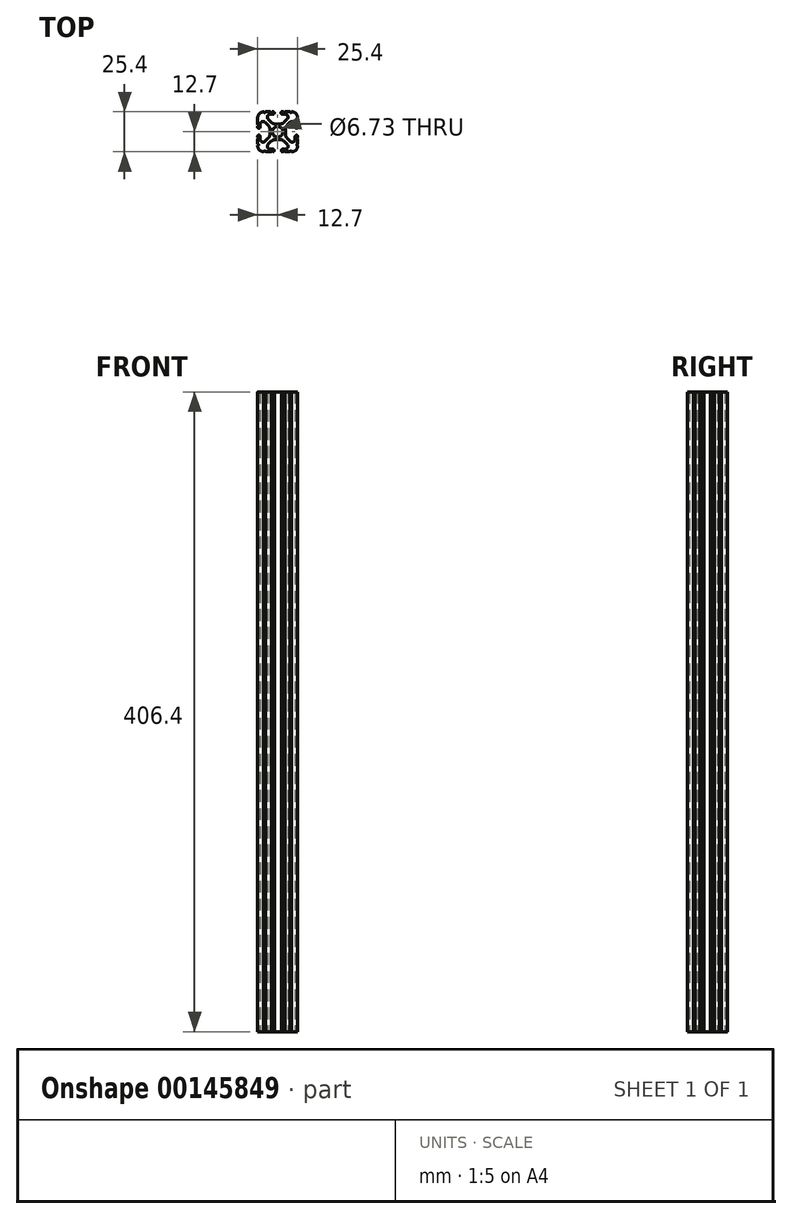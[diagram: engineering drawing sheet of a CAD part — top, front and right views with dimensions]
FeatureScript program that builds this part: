
annotation { "Feature Type Name" : "Feature", "Feature Type Description" : "" }
export const myFeature = defineFeature(function(context is Context, id is Id, definition is map)
    precondition{}
    {
        {
            var Q0;
            Q0=qCreatedBy(makeId("Top.planeOp"),FACE);
            var sketch = newSketch(context, id + "F0", { "sketchPlane" : qUnion([Q0])});
            skCircle(sketch, "E0", {"center": v(-12.7, 12.7) * mm, "radius": 3.36 * mm});
            skLineSegment(sketch, "E1.bottom", {"start": v(-11.24, 17.64) * mm, "end": v(-14.16, 17.64) * mm});
            skLineSegment(sketch, "E1.top", {"start": v(-11.24, 7.76) * mm, "end": v(-14.16, 7.76) * mm});
            skLineSegment(sketch, "E1.left", {"start": v(-7.76, 14.16) * mm, "end": v(-7.76, 11.24) * mm});
            skLineSegment(sketch, "E1.right", {"start": v(-17.64, 14.16) * mm, "end": v(-17.64, 11.24) * mm});
            skPoint(sketch, "E2.visualSharp", {"position": v(-25.4, 25.4) * mm});
            skPoint(sketch, "E3.visualSharp", {"position": v(0, 25.4) * mm});
            skPoint(sketch, "E4.visualSharp", {"position": v(0, 0) * mm});
            skPoint(sketch, "E5.visualSharp", {"position": v(-25.4, 0) * mm});
            skLineSegment(sketch, "E6.0", {"start": v(-18.7, 20.6) * mm, "end": v(-16.85, 18.76) * mm});
            skLineSegment(sketch, "E7.0", {"start": v(-20.6, 18.7) * mm, "end": v(-18.76, 16.85) * mm});
            skPoint(sketch, "E8.orphan", {"position": v(-23.85, 1.55) * mm});
            skPoint(sketch, "E9.orphan", {"position": v(-23.85, 23.85) * mm});
            skPoint(sketch, "E10.orphan", {"position": v(-1.55, 23.85) * mm});
            skPoint(sketch, "E11.orphan", {"position": v(-1.55, 1.55) * mm});
            skLineSegment(sketch, "E12", {"start": v(-8.55, 6.64) * mm, "end": v(-6.7, 4.8) * mm});
            skLineSegment(sketch, "E13.0", {"start": v(-18.7, 4.8) * mm, "end": v(-16.85, 6.64) * mm});
            skLineSegment(sketch, "E14.0", {"start": v(-20.6, 6.7) * mm, "end": v(-18.76, 8.55) * mm});
            skLineSegment(sketch, "E15.0", {"start": v(-8.55, 18.76) * mm, "end": v(-6.7, 20.6) * mm});
            skPoint(sketch, "E16.visualSharp", {"position": v(-23.85, 21.95) * mm});
            skArc(sketch, "E16.filletArc", {"start": v(-20.6, 18.7) * mm, "mid": v(-22.68, 19.1) * mm, "end": v(-23.85, 17.35) * mm});
            skPoint(sketch, "E17.visualSharp", {"position": v(-21.95, 23.85) * mm});
            skArc(sketch, "E17.filletArc", {"start": v(-17.35, 23.85) * mm, "mid": v(-19.1, 22.68) * mm, "end": v(-18.7, 20.6) * mm});
            skPoint(sketch, "E18.visualSharp", {"position": v(-5.34, 23.85) * mm});
            skLineSegment(sketch, "E19", {"start": v(-17.35, 23.85) * mm, "end": v(-15.58, 23.85) * mm});
            skLineSegment(sketch, "E20", {"start": v(-23.85, 17.35) * mm, "end": v(-23.85, 15.62) * mm});
            skLineSegment(sketch, "E21", {"start": v(-8.05, 1.55) * mm, "end": v(-9.78, 1.55) * mm});
            skArc(sketch, "E22.filletArc", {"start": v(-6.7, 20.6) * mm, "mid": v(-6.3, 22.68) * mm, "end": v(-8.05, 23.85) * mm});
            skPoint(sketch, "E23.visualSharp", {"position": v(-1.55, 3.45) * mm});
            skPoint(sketch, "E24.visualSharp", {"position": v(-3.45, 1.55) * mm});
            skArc(sketch, "E24.filletArc", {"start": v(-8.05, 1.55) * mm, "mid": v(-6.3, 2.73) * mm, "end": v(-6.7, 4.8) * mm});
            skArc(sketch, "E25.filletArc", {"start": v(-18.7, 4.8) * mm, "mid": v(-19.1, 2.73) * mm, "end": v(-17.35, 1.55) * mm});
            skArc(sketch, "E26.filletArc", {"start": v(-23.85, 8.05) * mm, "mid": v(-22.68, 6.3) * mm, "end": v(-20.6, 6.7) * mm});
            skLineSegment(sketch, "E27.bottom", {"start": v(-4.9, 0) * mm, "end": v(-8.05, 0) * mm});
            skLineSegment(sketch, "E27.top", {"start": v(-4.92, 25.4) * mm, "end": v(-8.05, 25.4) * mm});
            skLineSegment(sketch, "E27.left", {"start": v(0, 4.9) * mm, "end": v(0, 8.05) * mm});
            skLineSegment(sketch, "E27.right", {"start": v(-25.4, 4.9) * mm, "end": v(-25.4, 8.05) * mm});
            skArc(sketch, "E28.filletArc", {"start": v(-25.4, 3.81) * mm, "mid": v(-24.28, 1.12) * mm, "end": v(-21.59, 0) * mm});
            skArc(sketch, "E29.filletArc", {"start": v(-3.81, 0) * mm, "mid": v(-1.12, 1.12) * mm, "end": v(0, 3.8) * mm});
            skArc(sketch, "E30.filletArc", {"start": v(0, 21.59) * mm, "mid": v(-1.12, 24.28) * mm, "end": v(-3.8, 25.4) * mm});
            skArc(sketch, "E31.filletArc", {"start": v(-21.59, 25.4) * mm, "mid": v(-24.28, 24.28) * mm, "end": v(-25.4, 21.59) * mm});
            skPoint(sketch, "E32.newPointA", {"position": v(-17.64, 7.76) * mm});
            skArc(sketch, "E32.filletArc", {"start": v(-14.16, 7.76) * mm, "mid": v(-15.62, 7.47) * mm, "end": v(-16.85, 6.64) * mm});
            skPoint(sketch, "E33.newPointA", {"position": v(-7.76, 7.76) * mm});
            skArc(sketch, "E33.filletArc", {"start": v(-8.55, 6.64) * mm, "mid": v(-9.78, 7.47) * mm, "end": v(-11.24, 7.76) * mm});
            skArc(sketch, "E34.filletArc", {"start": v(-7.76, 11.24) * mm, "mid": v(-7.47, 9.78) * mm, "end": v(-6.64, 8.55) * mm});
            skArc(sketch, "E35.filletArc", {"start": v(-6.64, 16.85) * mm, "mid": v(-7.47, 15.62) * mm, "end": v(-7.76, 14.16) * mm});
            skPoint(sketch, "E36.newPointB", {"position": v(-7.76, 17.64) * mm});
            skArc(sketch, "E36.filletArc", {"start": v(-11.24, 17.64) * mm, "mid": v(-9.78, 17.93) * mm, "end": v(-8.55, 18.76) * mm});
            skPoint(sketch, "E37.newPointB", {"position": v(-17.64, 17.64) * mm});
            skArc(sketch, "E37.filletArc", {"start": v(-16.85, 18.76) * mm, "mid": v(-15.62, 17.93) * mm, "end": v(-14.16, 17.64) * mm});
            skArc(sketch, "E38.filletArc", {"start": v(-17.64, 14.16) * mm, "mid": v(-17.93, 15.62) * mm, "end": v(-18.76, 16.85) * mm});
            skArc(sketch, "E39.filletArc", {"start": v(-18.76, 8.55) * mm, "mid": v(-17.93, 9.78) * mm, "end": v(-17.64, 11.24) * mm});
            skLineSegment(sketch, "E40", {"start": v(-6.64, 8.55) * mm, "end": v(-4.8, 6.7) * mm});
            skPoint(sketch, "E41.visualSharp", {"position": v(-1.55, 21.95) * mm});
            skArc(sketch, "E42.filletArc", {"start": v(-4.8, 6.7) * mm, "mid": v(-2.73, 6.3) * mm, "end": v(-1.55, 8.05) * mm});
            skLineSegment(sketch, "E43", {"start": v(-1.55, 8.05) * mm, "end": v(-1.55, 9.78) * mm});
            skLineSegment(sketch, "E44", {"start": v(-6.64, 16.85) * mm, "end": v(-4.8, 18.7) * mm});
            skArc(sketch, "E45.filletArc", {"start": v(-1.55, 17.35) * mm, "mid": v(-2.73, 19.1) * mm, "end": v(-4.8, 18.7) * mm});
            skArc(sketch, "E46", {"start": v(-23.85, 9.78) * mm, "mid": v(-24.63, 10.56) * mm, "end": v(-25.4, 9.78) * mm});
            skArc(sketch, "E47", {"start": v(-25.4, 15.62) * mm, "mid": v(-24.63, 14.86) * mm, "end": v(-23.85, 15.62) * mm});
            skArc(sketch, "E48", {"start": v(-15.62, 23.85) * mm, "mid": v(-14.83, 24.63) * mm, "end": v(-15.62, 25.4) * mm});
            skArc(sketch, "E49", {"start": v(-9.78, 25.4) * mm, "mid": v(-10.6, 24.63) * mm, "end": v(-9.78, 23.85) * mm});
            skArc(sketch, "E50", {"start": v(-1.55, 15.62) * mm, "mid": v(-0.77, 14.88) * mm, "end": v(0, 15.62) * mm});
            skArc(sketch, "E51", {"start": v(0, 9.78) * mm, "mid": v(-0.77, 10.5) * mm, "end": v(-1.55, 9.78) * mm});
            skArc(sketch, "E52", {"start": v(-9.78, 1.55) * mm, "mid": v(-10.4, 0.77) * mm, "end": v(-9.78, 0) * mm});
            skArc(sketch, "E53", {"start": v(-15.62, 0) * mm, "mid": v(-14.85, 0.77) * mm, "end": v(-15.62, 1.55) * mm});
            skLineSegment(sketch, "E54.trimOffspring", {"start": v(-15.62, 1.55) * mm, "end": v(-17.35, 1.55) * mm});
            skLineSegment(sketch, "E55.trimOffspring", {"start": v(-16.7, 0) * mm, "end": v(-20.5, 0) * mm});
            skLineSegment(sketch, "E56.trimOffspring", {"start": v(-1.55, 15.62) * mm, "end": v(-1.55, 17.35) * mm});
            skLineSegment(sketch, "E57.trimOffspring", {"start": v(0, 15.62) * mm, "end": v(0, 16.26) * mm});
            skLineSegment(sketch, "E58.trimOffspring", {"start": v(-23.85, 9.78) * mm, "end": v(-23.85, 8.05) * mm});
            skLineSegment(sketch, "E59.trimOffspring", {"start": v(-25.4, 15.62) * mm, "end": v(-25.4, 16.26) * mm});
            skLineSegment(sketch, "E60.trimOffspring", {"start": v(-9.86, 23.85) * mm, "end": v(-8.05, 23.85) * mm});
            skLineSegment(sketch, "E61.trimOffspring", {"start": v(-15.58, 25.4) * mm, "end": v(-16.25, 25.4) * mm});
            skPoint(sketch, "E62.start.orphan", {"position": v(-15.62, 17.93) * mm});
            skPoint(sketch, "E63.start.orphan", {"position": v(-9.78, 17.93) * mm});
            skPoint(sketch, "E64.start.orphan", {"position": v(-7.47, 15.62) * mm});
            skPoint(sketch, "E65.start.orphan", {"position": v(-7.47, 9.78) * mm});
            skPoint(sketch, "E66.start.orphan", {"position": v(-17.93, 15.62) * mm});
            skPoint(sketch, "E67.start.orphan", {"position": v(-17.93, 9.78) * mm});
            skPoint(sketch, "E68.start.orphan", {"position": v(-9.78, 7.47) * mm});
            skPoint(sketch, "E69.start.orphan", {"position": v(-15.62, 7.47) * mm});
            skPoint(sketch, "E70.endSnap0", {"position": v(0, 18.6) * mm});
            skPoint(sketch, "E71.startSnap0", {"position": v(-1.55, 8.92) * mm});
            skArc(sketch, "E72", {"start": v(-4.92, 25.4) * mm, "mid": v(-4.37, 24.9) * mm, "end": v(-3.81, 25.4) * mm});
            skArc(sketch, "E73", {"start": v(-9.14, 25.4) * mm, "mid": v(-8.6, 24.86) * mm, "end": v(-8.05, 25.4) * mm});
            skArc(sketch, "E74", {"start": v(-17.35, 25.4) * mm, "mid": v(-16.8, 24.86) * mm, "end": v(-16.25, 25.4) * mm});
            skArc(sketch, "E75", {"start": v(-21.59, 25.4) * mm, "mid": v(-21.04, 24.85) * mm, "end": v(-20.49, 25.4) * mm});
            skLineSegment(sketch, "E76", {"start": v(-25.4, 21.59) * mm, "end": v(-25.4, 20.5) * mm});
            skArc(sketch, "E77", {"start": v(-25.4, 16.26) * mm, "mid": v(-24.84, 16.8) * mm, "end": v(-25.4, 17.35) * mm});
            skArc(sketch, "E78", {"start": v(-25.4, 8.05) * mm, "mid": v(-24.9, 8.6) * mm, "end": v(-25.4, 9.15) * mm});
            skArc(sketch, "E79", {"start": v(-25.4, 3.81) * mm, "mid": v(-24.85, 4.36) * mm, "end": v(-25.4, 4.9) * mm});
            skArc(sketch, "E80", {"start": v(-20.5, 0) * mm, "mid": v(-21.04, 0.55) * mm, "end": v(-21.59, 0) * mm});
            skArc(sketch, "E81", {"start": v(-15.62, 0) * mm, "mid": v(-16.16, 0.54) * mm, "end": v(-16.7, 0) * mm});
            skArc(sketch, "E82", {"start": v(-8.05, 0) * mm, "mid": v(-8.6, 0.55) * mm, "end": v(-9.15, 0) * mm});
            skArc(sketch, "E83", {"start": v(-3.81, 0) * mm, "mid": v(-4.35, 0.54) * mm, "end": v(-4.9, 0) * mm});
            skLineSegment(sketch, "E84.trimOffspring", {"start": v(-17.35, 25.4) * mm, "end": v(-20.49, 25.4) * mm});
            skLineSegment(sketch, "E85.trimOffspring", {"start": v(-25.4, 17.35) * mm, "end": v(-25.4, 21.59) * mm});
            skLineSegment(sketch, "E86.trimOffspring", {"start": v(-25.4, 9.15) * mm, "end": v(-25.4, 9.78) * mm});
            skLineSegment(sketch, "E87.trimOffspring", {"start": v(-9.15, 0) * mm, "end": v(-9.78, 0) * mm});
            skArc(sketch, "E88", {"start": v(0, 4.9) * mm, "mid": v(-0.54, 4.36) * mm, "end": v(0, 3.8) * mm});
            skArc(sketch, "E89", {"start": v(0, 9.15) * mm, "mid": v(-0.54, 8.6) * mm, "end": v(0, 8.05) * mm});
            skLineSegment(sketch, "E90.trimOffspring", {"start": v(0, 9.15) * mm, "end": v(0, 9.78) * mm});
            skArc(sketch, "E91", {"start": v(0, 21.59) * mm, "mid": v(-0.55, 21.04) * mm, "end": v(0, 20.5) * mm});
            skArc(sketch, "E92", {"start": v(0, 17.35) * mm, "mid": v(-0.55, 16.8) * mm, "end": v(0, 16.26) * mm});
            skLineSegment(sketch, "E93.trimOffspring", {"start": v(0, 17.35) * mm, "end": v(0, 20.5) * mm});
            skLineSegment(sketch, "E94.trimOffspring", {"start": v(-9.14, 25.4) * mm, "end": v(-9.86, 25.4) * mm});
            skSolve(sketch);
        }
        {
            var Q0;
            Q0=qSketchRegion(id+"F0",true);
            extrude(context, id + "F1", {"entities" : qUnion([Q0]), "depth" : 406.4 * mm});
        }
    });
